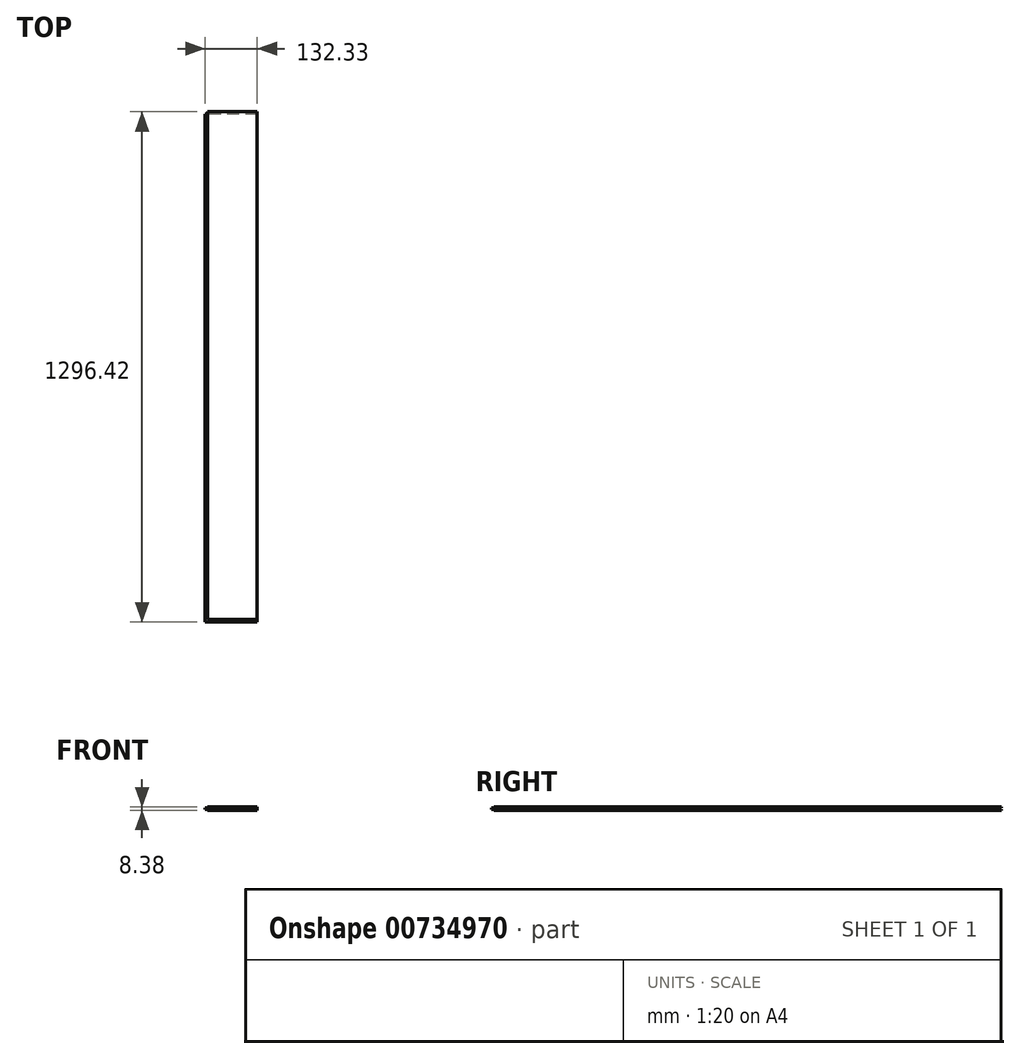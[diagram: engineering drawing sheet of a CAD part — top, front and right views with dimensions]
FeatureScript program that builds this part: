
annotation { "Feature Type Name" : "Feature", "Feature Type Description" : "" }
export const myFeature = defineFeature(function(context is Context, id is Id, definition is map)
    precondition{}
    {
        {
            var Q0;
            Q0=qCreatedBy(makeId("Front.planeOp"),FACE);
            var sketch = newSketch(context, id + "F0", { "sketchPlane" : qUnion([Q0])});
            skLineSegment(sketch, "E0.bottom", {"start": v(0, 0) * mm, "end": v(125.98, 0) * mm});
            skLineSegment(sketch, "E0.top", {"start": v(0, -8.38) * mm, "end": v(125.98, -8.38) * mm});
            skLineSegment(sketch, "E0.left", {"start": v(0, 0) * mm, "end": v(0, -8.38) * mm});
            skLineSegment(sketch, "E0.right", {"start": v(125.98, 0) * mm, "end": v(125.98, -8.38) * mm});
            skSolve(sketch);
        }
        {
            var Q0;
            Q0 = qSketchRegion(id + "F0", true);
            extrude(context, id + "F1", {"entities" : qUnion([Q0]), "depth" : 1290.07 * mm, "offsetDistance" : 25.4 * mm});
        }
        {
            var Q0;
            Q0=makeQuery(id+"F0.imprint","IMPRINT",FACE,{"disambiguationData":[TD([[makeQuery(id+"F0.imprint","IMPRINT",EDGE,{"derivedFrom":sQuery(id+"F0.wireOp",EDGE,"E0.bottom")}),-1.0]])]});
            var sketch = newSketch(context, id + "F2", { "sketchPlane" : qUnion([Q0])});
            skLineSegment(sketch, "E1.bottom", {"start": v(0, -2.8) * mm, "end": v(-6.35, -2.8) * mm});
            skLineSegment(sketch, "E1.top", {"start": v(0, -5.59) * mm, "end": v(-6.35, -5.59) * mm});
            skLineSegment(sketch, "E1.left", {"start": v(0, -2.8) * mm, "end": v(0, -5.59) * mm});
            skLineSegment(sketch, "E1.right", {"start": v(-6.35, -2.8) * mm, "end": v(-6.35, -5.59) * mm});
            skSolve(sketch);
        }
        {
            var Q0;
            Q0=makeQuery(id+"F2.imprint","IMPRINT",FACE,{"disambiguationData":[TD([[makeQuery(id+"F2.imprint","IMPRINT",EDGE,{"derivedFrom":sQuery(id+"F2.wireOp",EDGE,"E1.bottom")}),1.0]])]});
            extrude(context, id + "F3", {"entities" : qUnion([Q0]), "operationType" : NewBodyOperationType.ADD, "endBound" : BoundingType.THROUGH_ALL, "depth" : 25.4 * mm, "offsetDistance" : 25.4 * mm});
        }
        {
            var Q0;
            Q0=makeQuery(id+"F3.opExtrude","SWEPT_FACE",FACE,{"disambiguationData":[OSD([sQuery(id+"F2.wireOp",EDGE,"E1.right")])]});
            var sketch = newSketch(context, id + "F4", { "sketchPlane" : qUnion([Q0])});
            skLineSegment(sketch, "E2.bottom", {"start": v(1296.87, -2.8) * mm, "end": v(1296.42, -2.8) * mm});
            skLineSegment(sketch, "E2.top", {"start": v(1296.87, -5.59) * mm, "end": v(1296.42, -5.59) * mm});
            skLineSegment(sketch, "E2.left", {"start": v(1296.87, -2.8) * mm, "end": v(1296.87, -5.59) * mm});
            skLineSegment(sketch, "E2.right", {"start": v(1296.42, -2.8) * mm, "end": v(1296.42, -5.59) * mm});
            skSolve(sketch);
        }
        {
            var Q0;
            Q0 = qSketchRegion(id + "F4", true);
            extrude(context, id + "F5", {"entities" : qUnion([Q0]), "operationType" : NewBodyOperationType.REMOVE, "endBound" : BoundingType.THROUGH_ALL, "oppositeDirection" : true, "depth" : 25.4 * mm, "offsetDistance" : 25.4 * mm});
        }
        {
            var Q0;
            Q0=makeQuery(id+"F3.opExtrude","SWEPT_FACE",FACE,{"disambiguationData":[OSD([sQuery(id+"F2.wireOp",EDGE,"E1.right")])]});
            var sketch = newSketch(context, id + "F6", { "sketchPlane" : qUnion([Q0])});
            skLineSegment(sketch, "E3.bottom", {"start": v(1296.42, -2.8) * mm, "end": v(1290.07, -2.8) * mm});
            skLineSegment(sketch, "E3.top", {"start": v(1296.42, -5.59) * mm, "end": v(1290.07, -5.59) * mm});
            skLineSegment(sketch, "E3.left", {"start": v(1296.42, -2.8) * mm, "end": v(1296.42, -5.59) * mm});
            skLineSegment(sketch, "E3.right", {"start": v(1290.07, -2.8) * mm, "end": v(1290.07, -5.59) * mm});
            skSolve(sketch);
        }
        {
            var Q0;
            Q0 = qSketchRegion(id + "F6", true);
            var Q1;
            Q1=makeQuery(id+"F1.opExtrude","SWEPT_FACE",FACE,{"disambiguationData":[OSD([sQuery(id+"F0.wireOp",EDGE,"E0.right")])]});
            extrude(context, id + "F7", {"entities" : qUnion([Q0]), "operationType" : NewBodyOperationType.ADD, "endBound" : BoundingType.UP_TO_SURFACE, "oppositeDirection" : true, "depth" : 25.4 * mm, "endBoundEntityFace" : qUnion([Q1]), "offsetDistance" : 25.4 * mm});
        }
        {
            var Q0;
            Q0=makeQuery(id+"F3.boolean.opBoolean","MERGE",FACE,{"derivedFrom":[makeQuery(id+"F1.opExtrude","CAP_FACE",FACE,{"disambiguationData":[OSD([sQuery(id+"F0.wireOp",EDGE,"E0.bottom"),sQuery(id+"F0.wireOp",EDGE,"E0.top"),sQuery(id+"F0.wireOp",EDGE,"E0.left"),sQuery(id+"F0.wireOp",EDGE,"E0.right")])],"isStart":true}),makeQuery(id+"F3.opExtrude","CAP_FACE",FACE,{"disambiguationData":[OSD([sQuery(id+"F2.wireOp",EDGE,"E1.bottom"),sQuery(id+"F2.wireOp",EDGE,"E1.top"),sQuery(id+"F2.wireOp",EDGE,"E1.left"),sQuery(id+"F2.wireOp",EDGE,"E1.right")])],"isStart":true})]});
            var sketch = newSketch(context, id + "F8", { "sketchPlane" : qUnion([Q0])});
            skLineSegment(sketch, "E4.bottom", {"start": v(6.35, -2.8) * mm, "end": v(-125.98, -2.8) * mm});
            skLineSegment(sketch, "E4.top", {"start": v(6.35, -5.59) * mm, "end": v(-125.98, -5.59) * mm});
            skLineSegment(sketch, "E4.left", {"start": v(6.35, -2.8) * mm, "end": v(6.35, -5.59) * mm});
            skLineSegment(sketch, "E4.right", {"start": v(-125.98, -2.8) * mm, "end": v(-125.98, -5.59) * mm});
            skSolve(sketch);
        }
        {
            var Q0;
            {var subQ0=sQuery(id+"F8.wireOp",EDGE,"E4.left");Q0=makeQuery(id+"F8.imprint","IMPRINT",FACE,{"disambiguationData":[TD([[makeQuery(id+"F8.imprint","IMPRINT",EDGE,{"derivedFrom":subQ0}),-1.0]])]});}
            extrude(context, id + "F9", {"entities" : qUnion([Q0]), "operationType" : NewBodyOperationType.REMOVE, "oppositeDirection" : true, "depth" : 6.35 * mm, "offsetDistance" : 25.4 * mm});
        }
        {
            var Q0;
            Q0=makeQuery(id+"F1.opExtrude","SWEPT_BODY",BODY,{"disambiguationData":[OSD([sQuery(id+"F0.wireOp",EDGE,"E0.bottom"),sQuery(id+"F0.wireOp",EDGE,"E0.top"),sQuery(id+"F0.wireOp",EDGE,"E0.left"),sQuery(id+"F0.wireOp",EDGE,"E0.right")])]});
            transform(context, id + "F10", {"entities" : qUnion([Q0]), "transformType" : TransformType.TRANSLATION_3D, "dx" : 0 * mm, "dy" : 0 * mm, "dz" : 0 * mm, "makeCopy" : true});
        }
    });
